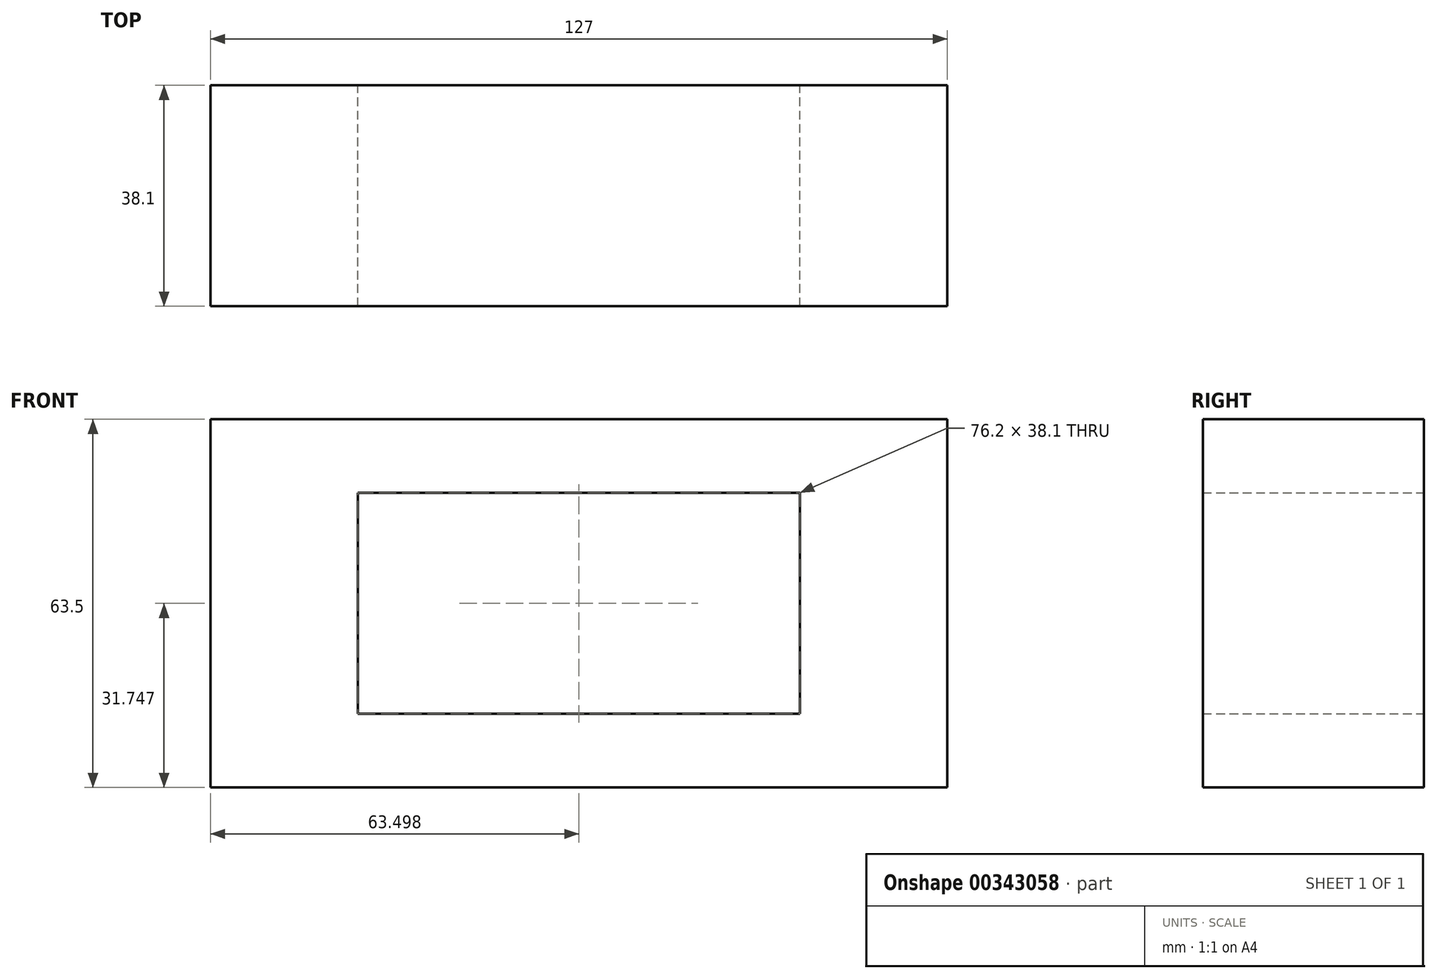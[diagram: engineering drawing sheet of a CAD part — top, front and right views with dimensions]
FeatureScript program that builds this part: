
annotation { "Feature Type Name" : "Feature", "Feature Type Description" : "" }
export const myFeature = defineFeature(function(context is Context, id is Id, definition is map)
    precondition{}
    {
        {
            var Q0;
            Q0=qCreatedBy(makeId("Front.planeOp"),FACE);
            var sketch = newSketch(context, id + "F0", { "sketchPlane" : qUnion([Q0])});
            skLineSegment(sketch, "E0", {"start": v(-73.95, -43.11) * mm, "end": v(53.05, -43.11) * mm});
            skLineSegment(sketch, "E1", {"start": v(-73.95, -43.11) * mm, "end": v(-73.95, 20.39) * mm});
            skLineSegment(sketch, "E2", {"start": v(-73.95, 20.39) * mm, "end": v(53.05, 20.39) * mm});
            skLineSegment(sketch, "E3", {"start": v(53.05, 20.39) * mm, "end": v(53.05, -43.11) * mm});
            skLineSegment(sketch, "E4", {"start": v(-48.55, 7.69) * mm, "end": v(-48.55, -30.41) * mm});
            skLineSegment(sketch, "E5", {"start": v(-48.55, 7.69) * mm, "end": v(27.65, 7.69) * mm});
            skLineSegment(sketch, "E6", {"start": v(-48.55, -30.41) * mm, "end": v(27.65, -30.41) * mm});
            skLineSegment(sketch, "E7", {"start": v(27.65, 7.69) * mm, "end": v(27.65, -30.41) * mm});
            skSolve(sketch);
        }
        {
            var Q0;
            Q0 = qSketchRegion(id + "F0", true);
            extrude(context, id + "F1", {"entities" : qUnion([Q0]), "depth" : 38.1 * mm});
        }
    });
